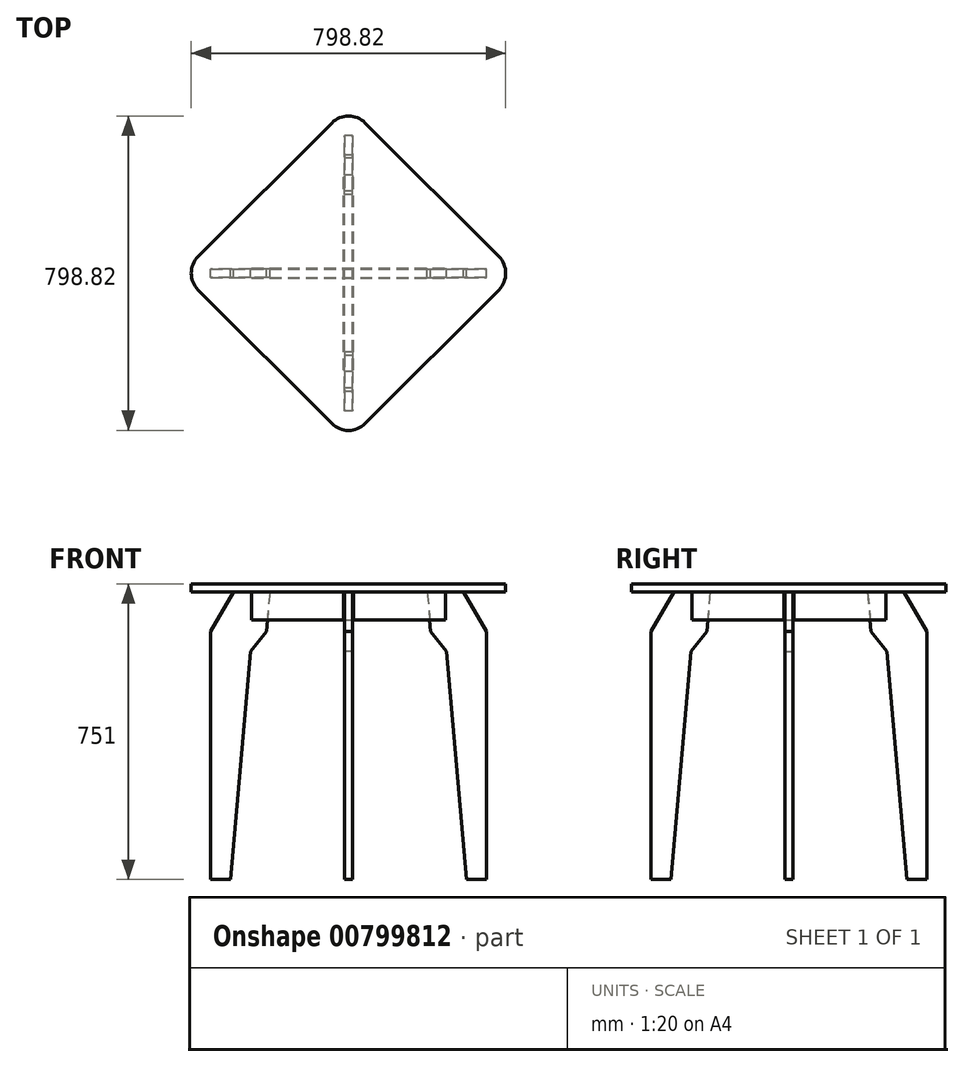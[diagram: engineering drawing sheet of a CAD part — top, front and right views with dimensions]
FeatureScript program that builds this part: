
annotation { "Feature Type Name" : "Feature", "Feature Type Description" : "" }
export const myFeature = defineFeature(function(context is Context, id is Id, definition is map)
    precondition{}
    {
        {
            var Q0;
            Q0=qCreatedBy(makeId("Front.planeOp"),FACE);
            var sketch = newSketch(context, id + "F0", { "sketchPlane" : qUnion([Q0])});
            skLineSegment(sketch, "E0", {"start": v(-350, 0) * mm, "end": v(-350, 730) * mm, "construction": true});
            skLineSegment(sketch, "E1", {"start": v(-350, 0) * mm, "end": v(-350, 630) * mm});
            skLineSegment(sketch, "E2", {"start": v(-350, 630) * mm, "end": v(-292.26, 730) * mm});
            skLineSegment(sketch, "E3", {"start": v(-292.26, 730) * mm, "end": v(-200, 730) * mm});
            skLineSegment(sketch, "E4", {"start": v(-200, 730) * mm, "end": v(-208.75, 630) * mm});
            skLineSegment(sketch, "E5", {"start": v(-208.75, 630) * mm, "end": v(-249.26, 580) * mm});
            skLineSegment(sketch, "E6", {"start": v(-249.26, 580) * mm, "end": v(-300, 0) * mm});
            skLineSegment(sketch, "E7", {"start": v(-300, 0) * mm, "end": v(-350, 0) * mm});
            skLineSegment(sketch, "E8.MirrorCS", {"start": v(350, 0) * mm, "end": v(350, 630) * mm});
            skLineSegment(sketch, "E9.MirrorCS", {"start": v(350, 0) * mm, "end": v(350, 730) * mm, "construction": true});
            skLineSegment(sketch, "E10.MirrorCS", {"start": v(249.26, 580) * mm, "end": v(300, 0) * mm});
            skLineSegment(sketch, "E11.MirrorCS", {"start": v(300, 0) * mm, "end": v(350, 0) * mm});
            skLineSegment(sketch, "E12.MirrorCS", {"start": v(350, 630) * mm, "end": v(292.26, 730) * mm});
            skLineSegment(sketch, "E13.MirrorCS", {"start": v(200, 730) * mm, "end": v(208.75, 630) * mm});
            skLineSegment(sketch, "E14.MirrorCS", {"start": v(292.26, 730) * mm, "end": v(200, 730) * mm});
            skLineSegment(sketch, "E15.MirrorCS", {"start": v(208.75, 630) * mm, "end": v(249.26, 580) * mm});
            skSolve(sketch);
        }
        {
            var Q0;
            Q0=makeQuery(id+"F0.imprint","IMPRINT",FACE,{"disambiguationData":[TD([[makeQuery(id+"F0.imprint","IMPRINT",EDGE,{"derivedFrom":sQuery(id+"F0.wireOp",EDGE,"E1")}),-1.0]])]});
            var Q1;
            Q1=makeQuery(id+"F0.imprint","IMPRINT",FACE,{"disambiguationData":[TD([[makeQuery(id+"F0.imprint","IMPRINT",EDGE,{"derivedFrom":sQuery(id+"F0.wireOp",EDGE,"E8.MirrorCS")}),1.0]])]});
            extrude(context, id + "F1", {"entities" : qUnion([Q0, Q1]), "endBound" : BoundingType.SYMMETRIC, "depth" : 21 * mm, "offsetDistance" : 25 * mm});
        }
        {
            var Q0;
            Q0=makeQuery(id+"F1.opExtrude","CAP_FACE",FACE,{"disambiguationData":[OSD([sQuery(id+"F0.wireOp",EDGE,"E1"),sQuery(id+"F0.wireOp",EDGE,"E2"),sQuery(id+"F0.wireOp",EDGE,"E3"),sQuery(id+"F0.wireOp",EDGE,"E4"),sQuery(id+"F0.wireOp",EDGE,"E5"),sQuery(id+"F0.wireOp",EDGE,"E6"),sQuery(id+"F0.wireOp",EDGE,"E7")])],"isStart":false});
            var sketch = newSketch(context, id + "F2", { "sketchPlane" : qUnion([Q0])});
            skLineSegment(sketch, "E16.bottom", {"start": v(-246.13, 730) * mm, "end": v(246.13, 730) * mm});
            skLineSegment(sketch, "E16.top", {"start": v(-246.13, 660) * mm, "end": v(246.13, 660) * mm});
            skLineSegment(sketch, "E16.left", {"start": v(-246.13, 730) * mm, "end": v(-246.13, 660) * mm});
            skLineSegment(sketch, "E16.right", {"start": v(246.13, 730) * mm, "end": v(246.13, 660) * mm});
            skSolve(sketch);
        }
        {
            var Q0;
            {var subQ3=sQuery(id+"F2.wireOp",EDGE,"E16.right");Q0=makeQuery(id+"F2.imprint","IMPRINT",FACE,{"disambiguationData":[TD([[makeQuery(id+"F2.imprint","IMPRINT",EDGE,{"derivedFrom":subQ3}),-1.0]])]});}
            var Q1;
            {var subQ3=sQuery(id+"F2.wireOp",EDGE,"E16.left");Q1=makeQuery(id+"F2.imprint","IMPRINT",FACE,{"disambiguationData":[TD([[makeQuery(id+"F2.imprint","IMPRINT",EDGE,{"derivedFrom":subQ3}),1.0]])]});}
            extrude(context, id + "F3", {"entities" : qUnion([Q0, Q1]), "depth" : 2 * mm, "offsetDistance" : 25 * mm});
        }
        {
            var Q0;
            Q0=makeQuery(id+"F3.opExtrude","SWEPT_BODY",BODY,{"disambiguationData":[OSD([sQuery(id+"F2.wireOp",EDGE,"E16.bottom"),sQuery(id+"F2.wireOp",EDGE,"E16.top"),sQuery(id+"F2.wireOp",EDGE,"E16.left"),sQuery(id+"F2.wireOp",EDGE,"E16.right")])]});
            var Q1;
            Q1=qCreatedBy(makeId("Front.planeOp"),FACE);
            mirror(context, id + "F4", {"entities" : qUnion([Q0]), "mirrorPlane" : qUnion([Q1])});
        }
        {
            var Q0;
            Q0=qCreatedBy(makeId("Front.planeOp"),FACE);
            var sketch = newSketch(context, id + "F5", { "sketchPlane" : qUnion([Q0])});
            skLineSegment(sketch, "E17", {"start": v(0, 0) * mm, "end": v(0, 566.12) * mm});
            skSolve(sketch);
        }
        {
            var Q0;
            Q0=makeQuery(id+"F1.opExtrude","SWEPT_BODY",BODY,{"disambiguationData":[OSD([sQuery(id+"F0.wireOp",EDGE,"E1"),sQuery(id+"F0.wireOp",EDGE,"E2"),sQuery(id+"F0.wireOp",EDGE,"E3"),sQuery(id+"F0.wireOp",EDGE,"E4"),sQuery(id+"F0.wireOp",EDGE,"E5"),sQuery(id+"F0.wireOp",EDGE,"E6"),sQuery(id+"F0.wireOp",EDGE,"E7")])]});
            var Q1;
            Q1=makeQuery(id+"F1.opExtrude","SWEPT_BODY",BODY,{"disambiguationData":[OSD([sQuery(id+"F0.wireOp",EDGE,"E8.MirrorCS"),sQuery(id+"F0.wireOp",EDGE,"E10.MirrorCS"),sQuery(id+"F0.wireOp",EDGE,"E11.MirrorCS"),sQuery(id+"F0.wireOp",EDGE,"E12.MirrorCS"),sQuery(id+"F0.wireOp",EDGE,"E13.MirrorCS"),sQuery(id+"F0.wireOp",EDGE,"E14.MirrorCS"),sQuery(id+"F0.wireOp",EDGE,"E15.MirrorCS")])]});
            var Q2;
            Q2=makeQuery(id+"F3.opExtrude","SWEPT_BODY",BODY,{"disambiguationData":[OSD([sQuery(id+"F2.wireOp",EDGE,"E16.bottom"),sQuery(id+"F2.wireOp",EDGE,"E16.top"),sQuery(id+"F2.wireOp",EDGE,"E16.left"),sQuery(id+"F2.wireOp",EDGE,"E16.right")])]});
            var Q3;
            Q3=makeQuery(id+"F4.opPattern","COPY",BODY,{"derivedFrom":makeQuery(id+"F3.opExtrude","SWEPT_BODY",BODY,{"disambiguationData":[OSD([sQuery(id+"F2.wireOp",EDGE,"E16.bottom"),sQuery(id+"F2.wireOp",EDGE,"E16.top"),sQuery(id+"F2.wireOp",EDGE,"E16.left"),sQuery(id+"F2.wireOp",EDGE,"E16.right")])]}),"instanceName":"1"});
            var Q4;
            Q4=sQuery(id+"F5.wireOp",EDGE,"E17");
            circularPattern(context, id + "F6", {"entities" : qUnion([Q0, Q1, Q2, Q3]), "axis" : qUnion([Q4]), "angle" : 360 * degree, "instanceCount" : 4, "equalSpace" : true});
        }
        {
            var Q0;
            Q0=makeQuery(id+"F1.opExtrude","SWEPT_FACE",FACE,{"disambiguationData":[OSD([sQuery(id+"F0.wireOp",EDGE,"E3")])]});
            var sketch = newSketch(context, id + "F7", { "sketchPlane" : qUnion([Q0])});
            skLineSegment(sketch, "E18", {"start": v(-424.26, 0) * mm, "end": v(0, 424.26) * mm});
            skLineSegment(sketch, "E19", {"start": v(0, 424.26) * mm, "end": v(424.26, 0) * mm});
            skLineSegment(sketch, "E20", {"start": v(424.26, 0) * mm, "end": v(0, -424.26) * mm});
            skLineSegment(sketch, "E21", {"start": v(0, -424.26) * mm, "end": v(-424.26, 0) * mm});
            skSolve(sketch);
        }
        {
            var Q0;
            Q0=makeQuery(id+"F7.imprint","IMPRINT",FACE,{"disambiguationData":[TD([[makeQuery(id+"F7.imprint","IMPRINT",EDGE,{"derivedFrom":sQuery(id+"F7.wireOp",EDGE,"E18")}),-1.0]])]});
            var Q1;
            {var subQ0=sQuery(id+"F0.wireOp",EDGE,"E3");Q1=makeQuery(id+"F7.imprint","IMPRINT",FACE,{"disambiguationData":[TD([[makeQuery(id+"F7.imprint","IMPRINT",EDGE,{"derivedFrom":makeQuery(id+"F1.opExtrude","CAP_EDGE",EDGE,{"disambiguationData":[OSD([subQ0])],"isStart":true})}),-1.0]])]});}
            extrude(context, id + "F8", {"entities" : qUnion([Q0, Q1]), "depth" : 21 * mm, "offsetDistance" : 25 * mm});
        }
        {
            var Q0;
            Q0=makeQuery(id+"F8.opExtrude","SWEPT_EDGE",EDGE,{"disambiguationData":[OSD([sQuery(id+"F7.wireOp",EDGE,"E20"),sQuery(id+"F7.wireOp",EDGE,"E21")])]});
            var Q1;
            Q1=makeQuery(id+"F8.opExtrude","SWEPT_EDGE",EDGE,{"disambiguationData":[OSD([sQuery(id+"F7.wireOp",EDGE,"E19"),sQuery(id+"F7.wireOp",EDGE,"E20")])]});
            var Q2;
            Q2=makeQuery(id+"F8.opExtrude","SWEPT_EDGE",EDGE,{"disambiguationData":[OSD([sQuery(id+"F7.wireOp",EDGE,"E18"),sQuery(id+"F7.wireOp",EDGE,"E21")])]});
            var Q3;
            Q3=makeQuery(id+"F8.opExtrude","SWEPT_EDGE",EDGE,{"disambiguationData":[OSD([sQuery(id+"F7.wireOp",EDGE,"E18"),sQuery(id+"F7.wireOp",EDGE,"E19")])]});
            fillet(context, id + "F9", {"entities" : qUnion([Q0, Q1, Q2, Q3]), "radius" : 60 * mm, "tangentPropagation" : true, "allowEdgeOverflow" : false});
        }
        {
            var Q0;
            Q0=makeQuery(id+"F6.opPattern","COPY",BODY,{"derivedFrom":makeQuery(id+"F1.opExtrude","SWEPT_BODY",BODY,{"disambiguationData":[OSD([sQuery(id+"F0.wireOp",EDGE,"E1"),sQuery(id+"F0.wireOp",EDGE,"E2"),sQuery(id+"F0.wireOp",EDGE,"E3"),sQuery(id+"F0.wireOp",EDGE,"E4"),sQuery(id+"F0.wireOp",EDGE,"E5"),sQuery(id+"F0.wireOp",EDGE,"E6"),sQuery(id+"F0.wireOp",EDGE,"E7")])]}),"instanceName":"2"});
            var Q1;
            Q1=makeQuery(id+"F6.opPattern","COPY",BODY,{"derivedFrom":makeQuery(id+"F1.opExtrude","SWEPT_BODY",BODY,{"disambiguationData":[OSD([sQuery(id+"F0.wireOp",EDGE,"E8.MirrorCS"),sQuery(id+"F0.wireOp",EDGE,"E10.MirrorCS"),sQuery(id+"F0.wireOp",EDGE,"E11.MirrorCS"),sQuery(id+"F0.wireOp",EDGE,"E12.MirrorCS"),sQuery(id+"F0.wireOp",EDGE,"E13.MirrorCS"),sQuery(id+"F0.wireOp",EDGE,"E14.MirrorCS"),sQuery(id+"F0.wireOp",EDGE,"E15.MirrorCS")])]}),"instanceName":"2"});
            var Q2;
            Q2=makeQuery(id+"F6.opPattern","COPY",BODY,{"derivedFrom":makeQuery(id+"F3.opExtrude","SWEPT_BODY",BODY,{"disambiguationData":[OSD([sQuery(id+"F2.wireOp",EDGE,"E16.bottom"),sQuery(id+"F2.wireOp",EDGE,"E16.top"),sQuery(id+"F2.wireOp",EDGE,"E16.left"),sQuery(id+"F2.wireOp",EDGE,"E16.right")])]}),"instanceName":"2"});
            var Q3;
            Q3=makeQuery(id+"F6.opPattern","COPY",BODY,{"derivedFrom":makeQuery(id+"F4.opPattern","COPY",BODY,{"derivedFrom":makeQuery(id+"F3.opExtrude","SWEPT_BODY",BODY,{"disambiguationData":[OSD([sQuery(id+"F2.wireOp",EDGE,"E16.bottom"),sQuery(id+"F2.wireOp",EDGE,"E16.top"),sQuery(id+"F2.wireOp",EDGE,"E16.left"),sQuery(id+"F2.wireOp",EDGE,"E16.right")])]}),"instanceName":"1"}),"instanceName":"2"});
            var Q4;
            Q4=makeQuery(id+"F6.opPattern","COPY",BODY,{"derivedFrom":makeQuery(id+"F1.opExtrude","SWEPT_BODY",BODY,{"disambiguationData":[OSD([sQuery(id+"F0.wireOp",EDGE,"E1"),sQuery(id+"F0.wireOp",EDGE,"E2"),sQuery(id+"F0.wireOp",EDGE,"E3"),sQuery(id+"F0.wireOp",EDGE,"E4"),sQuery(id+"F0.wireOp",EDGE,"E5"),sQuery(id+"F0.wireOp",EDGE,"E6"),sQuery(id+"F0.wireOp",EDGE,"E7")])]}),"instanceName":"3"});
            var Q5;
            Q5=makeQuery(id+"F6.opPattern","COPY",BODY,{"derivedFrom":makeQuery(id+"F1.opExtrude","SWEPT_BODY",BODY,{"disambiguationData":[OSD([sQuery(id+"F0.wireOp",EDGE,"E8.MirrorCS"),sQuery(id+"F0.wireOp",EDGE,"E10.MirrorCS"),sQuery(id+"F0.wireOp",EDGE,"E11.MirrorCS"),sQuery(id+"F0.wireOp",EDGE,"E12.MirrorCS"),sQuery(id+"F0.wireOp",EDGE,"E13.MirrorCS"),sQuery(id+"F0.wireOp",EDGE,"E14.MirrorCS"),sQuery(id+"F0.wireOp",EDGE,"E15.MirrorCS")])]}),"instanceName":"3"});
            var Q6;
            Q6=makeQuery(id+"F6.opPattern","COPY",BODY,{"derivedFrom":makeQuery(id+"F3.opExtrude","SWEPT_BODY",BODY,{"disambiguationData":[OSD([sQuery(id+"F2.wireOp",EDGE,"E16.bottom"),sQuery(id+"F2.wireOp",EDGE,"E16.top"),sQuery(id+"F2.wireOp",EDGE,"E16.left"),sQuery(id+"F2.wireOp",EDGE,"E16.right")])]}),"instanceName":"3"});
            var Q7;
            Q7=makeQuery(id+"F6.opPattern","COPY",BODY,{"derivedFrom":makeQuery(id+"F4.opPattern","COPY",BODY,{"derivedFrom":makeQuery(id+"F3.opExtrude","SWEPT_BODY",BODY,{"disambiguationData":[OSD([sQuery(id+"F2.wireOp",EDGE,"E16.bottom"),sQuery(id+"F2.wireOp",EDGE,"E16.top"),sQuery(id+"F2.wireOp",EDGE,"E16.left"),sQuery(id+"F2.wireOp",EDGE,"E16.right")])]}),"instanceName":"1"}),"instanceName":"3"});
            deleteBodies(context, id + "F10", {"entities" : qUnion([Q0, Q1, Q2, Q3, Q4, Q5, Q6, Q7])});
        }
    });
